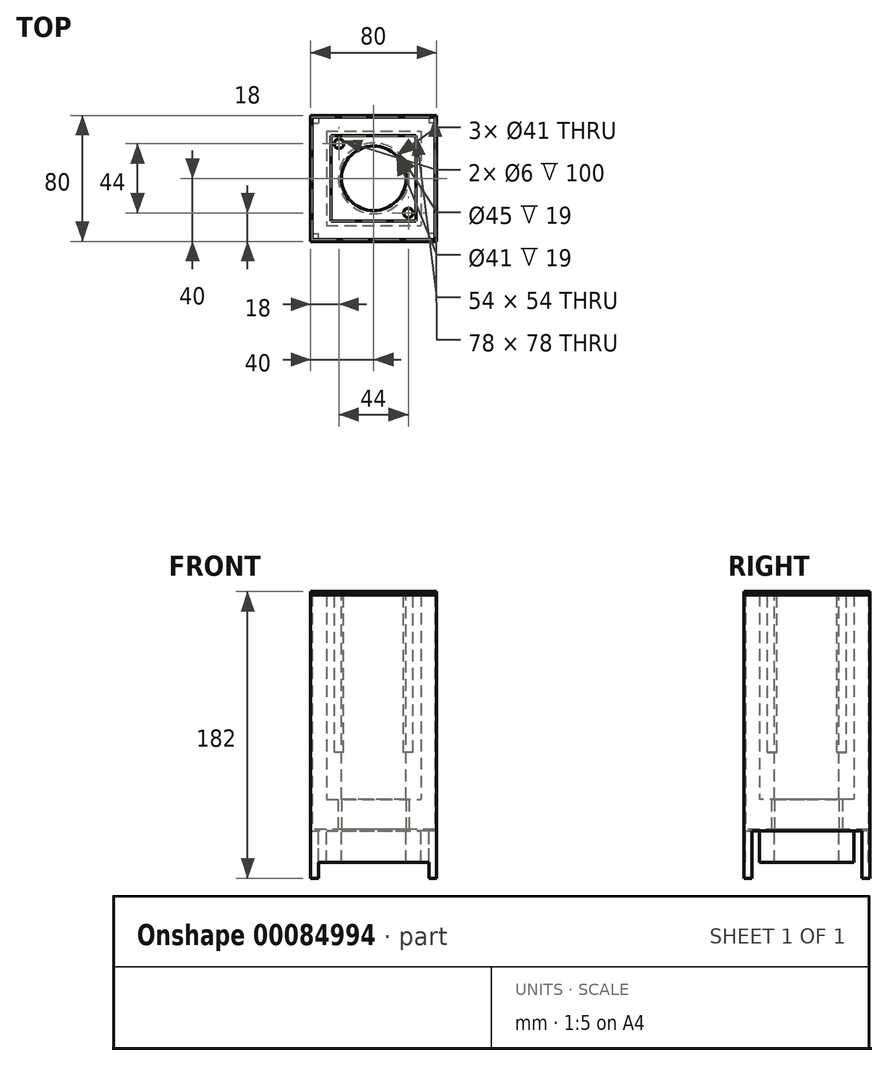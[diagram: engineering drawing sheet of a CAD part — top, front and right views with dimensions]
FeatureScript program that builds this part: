
annotation { "Feature Type Name" : "Feature", "Feature Type Description" : "" }
export const myFeature = defineFeature(function(context is Context, id is Id, definition is map)
    precondition{}
    {
        {
            var Q0;
            Q0=qCreatedBy(makeId("Top.planeOp"),FACE);
            var sketch = newSketch(context, id + "F0", { "sketchPlane" : qUnion([Q0])});
            skLineSegment(sketch, "E0.bottom", {"start": v(-30, 30) * mm, "end": v(30, 30) * mm});
            skLineSegment(sketch, "E0.top", {"start": v(-30, -30) * mm, "end": v(30, -30) * mm});
            skLineSegment(sketch, "E0.left", {"start": v(-30, 30) * mm, "end": v(-30, -30) * mm});
            skLineSegment(sketch, "E0.right", {"start": v(30, 30) * mm, "end": v(30, -30) * mm});
            skSolve(sketch);
        }
        {
            var Q0;
            Q0 = qSketchRegion(id + "F0", true);
            extrude(context, id + "F1", {"entities" : qUnion([Q0]), "depth" : 130 * mm});
        }
        {
            var Q0;
            Q0=makeQuery(id+"F1.opExtrude","CAP_FACE",FACE,{"disambiguationData":[OSD([sQuery(id+"F0.wireOp",EDGE,"E0.bottom"),sQuery(id+"F0.wireOp",EDGE,"E0.top"),sQuery(id+"F0.wireOp",EDGE,"E0.left"),sQuery(id+"F0.wireOp",EDGE,"E0.right")])],"isStart":false});
            var sketch = newSketch(context, id + "F2", { "sketchPlane" : qUnion([Q0])});
            skCircle(sketch, "E1", {"center": v(0, 0) * mm, "radius": 20.5 * mm});
            skSolve(sketch);
        }
        {
            var Q0;
            Q0=makeQuery(id+"F2.imprint","IMPRINT",FACE,{"disambiguationData":[TD([[makeQuery(id+"F2.imprint","IMPRINT",EDGE,{"derivedFrom":sQuery(id+"F2.wireOp",EDGE,"E1")}),1.0]])]});
            extrude(context, id + "F3", {"entities" : qUnion([Q0]), "operationType" : NewBodyOperationType.REMOVE, "oppositeDirection" : true, "depth" : 150 * mm});
        }
        {
            var Q0;
            Q0=makeQuery(id+"F1.opExtrude","CAP_FACE",FACE,{"disambiguationData":[OSD([sQuery(id+"F0.wireOp",EDGE,"E0.bottom"),sQuery(id+"F0.wireOp",EDGE,"E0.top"),sQuery(id+"F0.wireOp",EDGE,"E0.left"),sQuery(id+"F0.wireOp",EDGE,"E0.right")])],"isStart":false});
            var sketch = newSketch(context, id + "F4", { "sketchPlane" : qUnion([Q0])});
            skCircle(sketch, "E2", {"center": v(22, -22) * mm, "radius": 3 * mm});
            skCircle(sketch, "E3", {"center": v(-22, 22) * mm, "radius": 3 * mm});
            skSolve(sketch);
        }
        {
            var Q0;
            Q0=makeQuery(id+"F4.imprint","IMPRINT",FACE,{"disambiguationData":[TD([[makeQuery(id+"F4.imprint","IMPRINT",EDGE,{"derivedFrom":sQuery(id+"F4.wireOp",EDGE,"E3")}),1.0]])]});
            var Q1;
            Q1=makeQuery(id+"F4.imprint","IMPRINT",FACE,{"disambiguationData":[TD([[makeQuery(id+"F4.imprint","IMPRINT",EDGE,{"derivedFrom":sQuery(id+"F4.wireOp",EDGE,"E2")}),1.0]])]});
            extrude(context, id + "F5", {"entities" : qUnion([Q0, Q1]), "operationType" : NewBodyOperationType.REMOVE, "oppositeDirection" : true, "depth" : 100 * mm});
        }
        {
            var Q0;
            Q0 = qSketchRegion(id + "F4", true);
            extrude(context, id + "F6", {"entities" : qUnion([Q0]), "oppositeDirection" : true, "depth" : 100 * mm});
        }
        {
            var Q0;
            Q0=qCreatedBy(makeId("Top.planeOp"),FACE);
            var sketch = newSketch(context, id + "F7", { "sketchPlane" : qUnion([Q0])});
            skLineSegment(sketch, "E4.bottom", {"start": v(40, 40) * mm, "end": v(-40, 40) * mm});
            skLineSegment(sketch, "E4.top", {"start": v(40, -40) * mm, "end": v(-40, -40) * mm});
            skLineSegment(sketch, "E4.left", {"start": v(40, 40) * mm, "end": v(40, -40) * mm});
            skLineSegment(sketch, "E4.right", {"start": v(-40, 40) * mm, "end": v(-40, -40) * mm});
            skSolve(sketch);
        }
        {
            var Q0;
            Q0=makeQuery(id+"F7.imprint","IMPRINT",FACE,{"disambiguationData":[TD([[makeQuery(id+"F7.imprint","IMPRINT",EDGE,{"derivedFrom":sQuery(id+"F7.wireOp",EDGE,"E4.bottom")}),1.0]])]});
            extrude(context, id + "F8", {"entities" : qUnion([Q0]), "depth" : 130 * mm, "hasSecondDirection" : true, "secondDirectionOppositeDirection" : true, "secondDirectionDepth" : 20 * mm});
        }
        {
            var Q0;
            Q0=makeQuery(id+"F8.opExtrude","CAP_FACE",FACE,{"disambiguationData":[OSD([sQuery(id+"F7.wireOp",EDGE,"E4.bottom"),sQuery(id+"F7.wireOp",EDGE,"E4.top"),sQuery(id+"F7.wireOp",EDGE,"E4.left"),sQuery(id+"F7.wireOp",EDGE,"E4.right")])],"isStart":false});
            shell(context, id + "F9", {"entities" : qUnion([Q0]), "thickness" : 1 * mm});
        }
        {
            var Q0;
            Q0=makeQuery(id+"F8.opExtrude","CAP_FACE",FACE,{"disambiguationData":[OSD([sQuery(id+"F7.wireOp",EDGE,"E4.bottom"),sQuery(id+"F7.wireOp",EDGE,"E4.top"),sQuery(id+"F7.wireOp",EDGE,"E4.left"),sQuery(id+"F7.wireOp",EDGE,"E4.right")])],"isStart":true});
            var sketch = newSketch(context, id + "F10", { "sketchPlane" : qUnion([Q0])});
            skCircle(sketch, "E5", {"center": v(0, 0) * mm, "radius": 20.5 * mm});
            skSolve(sketch);
        }
        {
            var Q0;
            Q0=makeQuery(id+"F10.imprint","IMPRINT",FACE,{"disambiguationData":[TD([[makeQuery(id+"F10.imprint","IMPRINT",EDGE,{"derivedFrom":sQuery(id+"F10.wireOp",EDGE,"E5")}),1.0]])]});
            extrude(context, id + "F11", {"entities" : qUnion([Q0]), "operationType" : NewBodyOperationType.REMOVE, "oppositeDirection" : true, "depth" : 25 * mm});
        }
        {
            var Q0;
            Q0=makeQuery(id+"F9.opShell","OFFSET_FACE",FACE,{"disambiguationData":[OSD([sQuery(id+"F7.wireOp",EDGE,"E4.bottom"),sQuery(id+"F7.wireOp",EDGE,"E4.top"),sQuery(id+"F7.wireOp",EDGE,"E4.left"),sQuery(id+"F7.wireOp",EDGE,"E4.right")])]});
            var sketch = newSketch(context, id + "F12", { "sketchPlane" : qUnion([Q0])});
            skCircle(sketch, "E6", {"center": v(0, 0) * mm, "radius": 22.5 * mm});
            skCircle(sketch, "E7", {"center": v(0, 0) * mm, "radius": 20.5 * mm});
            skSolve(sketch);
        }
        {
            var Q0;
            Q0=makeQuery(id+"F12.imprint","IMPRINT",FACE,{"disambiguationData":[TD([[makeQuery(id+"F12.imprint","IMPRINT",EDGE,{"derivedFrom":sQuery(id+"F12.wireOp",EDGE,"E6")}),1.0]])]});
            extrude(context, id + "F13", {"entities" : qUnion([Q0]), "depth" : 19 * mm});
        }
        {
            var Q0;
            Q0=makeQuery(id+"F8.opExtrude","CAP_FACE",FACE,{"disambiguationData":[OSD([sQuery(id+"F7.wireOp",EDGE,"E4.bottom"),sQuery(id+"F7.wireOp",EDGE,"E4.top"),sQuery(id+"F7.wireOp",EDGE,"E4.left"),sQuery(id+"F7.wireOp",EDGE,"E4.right")])],"isStart":true});
            var sketch = newSketch(context, id + "F14", { "sketchPlane" : qUnion([Q0])});
            skLineSegment(sketch, "E8.0", {"start": v(30, -30) * mm, "end": v(30, 30) * mm});
            skLineSegment(sketch, "E8.1", {"start": v(-30, -30) * mm, "end": v(30, -30) * mm});
            skLineSegment(sketch, "E8.2", {"start": v(-30, 30) * mm, "end": v(-30, -30) * mm});
            skLineSegment(sketch, "E8.3", {"start": v(30, 30) * mm, "end": v(-30, 30) * mm});
            skSolve(sketch);
        }
        {
            var Q0;
            Q0=makeQuery(id+"F14.imprint","IMPRINT",FACE,{"disambiguationData":[TD([[makeQuery(id+"F14.imprint","IMPRINT",EDGE,{"derivedFrom":sQuery(id+"F14.wireOp",EDGE,"E8.0")}),1.0]])]});
            var Q1;
            Q1=makeQuery(id+"F14.imprint","IMPRINT",FACE,{"disambiguationData":[TD([[makeQuery(id+"F14.imprint","IMPRINT",EDGE,{"derivedFrom":makeQuery(id+"F11.boolean.opBoolean","COPY",EDGE,{"derivedFrom":makeQuery(id+"F11.opExtrude","CAP_EDGE",EDGE,{"disambiguationData":[OSD([sQuery(id+"F10.wireOp",EDGE,"E5")])],"isStart":true})})}),1.0]])]});
            extrude(context, id + "F15", {"entities" : qUnion([Q0, Q1]), "depth" : 20 * mm});
        }
        {
            var Q0;
            Q0=makeQuery(id+"F8.opExtrude","CAP_FACE",FACE,{"disambiguationData":[OSD([sQuery(id+"F7.wireOp",EDGE,"E4.bottom"),sQuery(id+"F7.wireOp",EDGE,"E4.top"),sQuery(id+"F7.wireOp",EDGE,"E4.left"),sQuery(id+"F7.wireOp",EDGE,"E4.right")])],"isStart":true});
            var sketch = newSketch(context, id + "F16", { "sketchPlane" : qUnion([Q0])});
            skLineSegment(sketch, "E9.bottom", {"start": v(40, -40) * mm, "end": v(35, -40) * mm});
            skLineSegment(sketch, "E9.top", {"start": v(40, -35) * mm, "end": v(35, -35) * mm});
            skLineSegment(sketch, "E9.left", {"start": v(40, -40) * mm, "end": v(40, -35) * mm});
            skLineSegment(sketch, "E9.right", {"start": v(35, -40) * mm, "end": v(35, -35) * mm});
            skLineSegment(sketch, "E10.bottom", {"start": v(-40, -40) * mm, "end": v(-35, -40) * mm});
            skLineSegment(sketch, "E10.top", {"start": v(-40, -35) * mm, "end": v(-35, -35) * mm});
            skLineSegment(sketch, "E10.left", {"start": v(-40, -40) * mm, "end": v(-40, -35) * mm});
            skLineSegment(sketch, "E10.right", {"start": v(-35, -40) * mm, "end": v(-35, -35) * mm});
            skLineSegment(sketch, "E11.bottom", {"start": v(-40, 40) * mm, "end": v(-35, 40) * mm});
            skLineSegment(sketch, "E11.top", {"start": v(-40, 35) * mm, "end": v(-35, 35) * mm});
            skLineSegment(sketch, "E11.left", {"start": v(-40, 40) * mm, "end": v(-40, 35) * mm});
            skLineSegment(sketch, "E11.right", {"start": v(-35, 40) * mm, "end": v(-35, 35) * mm});
            skLineSegment(sketch, "E12.bottom", {"start": v(40, 40) * mm, "end": v(35, 40) * mm});
            skLineSegment(sketch, "E12.top", {"start": v(40, 35) * mm, "end": v(35, 35) * mm});
            skLineSegment(sketch, "E12.left", {"start": v(40, 40) * mm, "end": v(40, 35) * mm});
            skLineSegment(sketch, "E12.right", {"start": v(35, 40) * mm, "end": v(35, 35) * mm});
            skLineSegment(sketch, "E13.bottom", {"start": v(40, -35) * mm, "end": v(37.5, -35) * mm});
            skLineSegment(sketch, "E13.top", {"start": v(40, 35) * mm, "end": v(37.5, 35) * mm});
            skLineSegment(sketch, "E14.bottom", {"start": v(-40, -35) * mm, "end": v(-39, -35) * mm});
            skLineSegment(sketch, "E14.top", {"start": v(-40, 35) * mm, "end": v(-39, 35) * mm});
            skLineSegment(sketch, "E14.left", {"start": v(-40, -35) * mm, "end": v(-40, 35) * mm});
            skLineSegment(sketch, "E14.right", {"start": v(-39, -35) * mm, "end": v(-39, 35) * mm});
            skLineSegment(sketch, "E15.bottom", {"start": v(40, 35) * mm, "end": v(39, 35) * mm});
            skLineSegment(sketch, "E15.top", {"start": v(40, -35) * mm, "end": v(39, -35) * mm});
            skLineSegment(sketch, "E15.left", {"start": v(40, 35) * mm, "end": v(40, -35) * mm});
            skLineSegment(sketch, "E15.right", {"start": v(39, 35) * mm, "end": v(39, -35) * mm});
            skLineSegment(sketch, "E16.bottom", {"start": v(-35, -40) * mm, "end": v(35, -40) * mm});
            skLineSegment(sketch, "E16.top", {"start": v(-35, -39) * mm, "end": v(35, -39) * mm});
            skLineSegment(sketch, "E16.left", {"start": v(-35, -40) * mm, "end": v(-35, -39) * mm});
            skLineSegment(sketch, "E16.right", {"start": v(35, -40) * mm, "end": v(35, -39) * mm});
            skLineSegment(sketch, "E17.bottom", {"start": v(35, 40) * mm, "end": v(-35, 40) * mm});
            skLineSegment(sketch, "E17.top", {"start": v(35, 39) * mm, "end": v(-35, 39) * mm});
            skLineSegment(sketch, "E17.left", {"start": v(35, 40) * mm, "end": v(35, 39) * mm});
            skLineSegment(sketch, "E17.right", {"start": v(-35, 40) * mm, "end": v(-35, 39) * mm});
            skSolve(sketch);
        }
        {
            var Q0;
            Q0=makeQuery(id+"F16.imprint","IMPRINT",FACE,{"disambiguationData":[TD([[makeQuery(id+"F16.imprint","IMPRINT",EDGE,{"derivedFrom":sQuery(id+"F16.wireOp",EDGE,"E9.bottom")}),-1.0]])]});
            var Q1;
            Q1=makeQuery(id+"F16.imprint","IMPRINT",FACE,{"disambiguationData":[TD([[makeQuery(id+"F16.imprint","IMPRINT",EDGE,{"derivedFrom":sQuery(id+"F16.wireOp",EDGE,"E10.bottom")}),-1.0]])]});
            var Q2;
            Q2=makeQuery(id+"F16.imprint","IMPRINT",FACE,{"disambiguationData":[TD([[makeQuery(id+"F16.imprint","IMPRINT",EDGE,{"derivedFrom":sQuery(id+"F16.wireOp",EDGE,"E11.bottom")}),1.0]])]});
            var Q3;
            Q3=makeQuery(id+"F16.imprint","IMPRINT",FACE,{"disambiguationData":[TD([[makeQuery(id+"F16.imprint","IMPRINT",EDGE,{"derivedFrom":sQuery(id+"F16.wireOp",EDGE,"E12.bottom")}),1.0]])]});
            extrude(context, id + "F17", {"entities" : qUnion([Q0, Q1, Q2, Q3]), "operationType" : NewBodyOperationType.ADD, "depth" : 30 * mm});
        }
        {
            var Q0;
            Q0=makeQuery(id+"F16.imprint","IMPRINT",FACE,{"disambiguationData":[TD([[makeQuery(id+"F16.imprint","IMPRINT",EDGE,{"derivedFrom":sQuery(id+"F16.wireOp",EDGE,"E15.bottom")}),1.0]])]});
            var Q1;
            Q1=makeQuery(id+"F16.imprint","IMPRINT",FACE,{"disambiguationData":[TD([[makeQuery(id+"F16.imprint","IMPRINT",EDGE,{"derivedFrom":sQuery(id+"F16.wireOp",EDGE,"E16.bottom")}),-1.0]])]});
            var Q2;
            Q2=makeQuery(id+"F16.imprint","IMPRINT",FACE,{"disambiguationData":[TD([[makeQuery(id+"F16.imprint","IMPRINT",EDGE,{"derivedFrom":sQuery(id+"F16.wireOp",EDGE,"E14.bottom")}),1.0]])]});
            var Q3;
            Q3=makeQuery(id+"F16.imprint","IMPRINT",FACE,{"disambiguationData":[TD([[makeQuery(id+"F16.imprint","IMPRINT",EDGE,{"derivedFrom":sQuery(id+"F16.wireOp",EDGE,"E17.bottom")}),1.0]])]});
            extrude(context, id + "F18", {"entities" : qUnion([Q0, Q1, Q2, Q3]), "operationType" : NewBodyOperationType.ADD, "depth" : 20 * mm});
        }
        {
            var Q0;
            Q0=makeQuery(id+"F9.opShell","OFFSET_FACE",FACE,{"disambiguationData":[OSD([sQuery(id+"F7.wireOp",EDGE,"E4.bottom"),sQuery(id+"F7.wireOp",EDGE,"E4.top"),sQuery(id+"F7.wireOp",EDGE,"E4.left"),sQuery(id+"F7.wireOp",EDGE,"E4.right")])]});
            extrude(context, id + "F19", {"entities" : qUnion([Q0]), "depth" : 149 * mm});
        }
        {
            var Q0;
            Q0=makeQuery(id+"F15.opExtrude","SWEPT_BODY",BODY,{"disambiguationData":[OSD([sQuery(id+"F14.wireOp",EDGE,"E8.0"),sQuery(id+"F14.wireOp",EDGE,"E8.1"),sQuery(id+"F14.wireOp",EDGE,"E8.2"),sQuery(id+"F14.wireOp",EDGE,"E8.3")])]});
            var Q1;
            Q1=makeQuery(id+"F13.opExtrude","SWEPT_BODY",BODY,{"disambiguationData":[OSD([sQuery(id+"F12.wireOp",EDGE,"E6"),sQuery(id+"F12.wireOp",EDGE,"E7")])]});
            var Q2;
            Q2=makeQuery(id+"F6.opExtrude","SWEPT_BODY",BODY,{"disambiguationData":[OSD([sQuery(id+"F4.wireOp",EDGE,"E3")])]});
            var Q3;
            Q3=makeQuery(id+"F8.opExtrude","SWEPT_BODY",BODY,{"disambiguationData":[OSD([sQuery(id+"F7.wireOp",EDGE,"E4.bottom"),sQuery(id+"F7.wireOp",EDGE,"E4.top"),sQuery(id+"F7.wireOp",EDGE,"E4.left"),sQuery(id+"F7.wireOp",EDGE,"E4.right")])]});
            var Q4;
            Q4=makeQuery(id+"F6.opExtrude","SWEPT_BODY",BODY,{"disambiguationData":[OSD([sQuery(id+"F4.wireOp",EDGE,"E2")])]});
            var Q5;
            Q5=makeQuery(id+"F1.opExtrude","SWEPT_BODY",BODY,{"disambiguationData":[OSD([sQuery(id+"F0.wireOp",EDGE,"E0.bottom"),sQuery(id+"F0.wireOp",EDGE,"E0.top"),sQuery(id+"F0.wireOp",EDGE,"E0.left"),sQuery(id+"F0.wireOp",EDGE,"E0.right")])]});
            var Q6;
            Q6=makeQuery(id+"F19.opExtrude","SWEPT_BODY",BODY,{"disambiguationData":[OSD([sQuery(id+"F7.wireOp",EDGE,"E4.bottom"),sQuery(id+"F7.wireOp",EDGE,"E4.top"),sQuery(id+"F7.wireOp",EDGE,"E4.left"),sQuery(id+"F7.wireOp",EDGE,"E4.right")])]});
            booleanBodies(context, id + "F20", {"operationType" : BooleanOperationType.SUBTRACTION, "tools" : qUnion([Q0, Q1, Q2, Q3, Q4, Q5]), "targets" : qUnion([Q6]), "keepTools" : true});
        }
        {
            var Q0;
            Q0=makeQuery(id+"F19.opExtrude","CAP_FACE",FACE,{"disambiguationData":[OSD([sQuery(id+"F7.wireOp",EDGE,"E4.bottom"),sQuery(id+"F7.wireOp",EDGE,"E4.top"),sQuery(id+"F7.wireOp",EDGE,"E4.left"),sQuery(id+"F7.wireOp",EDGE,"E4.right")])],"isStart":false});
            var sketch = newSketch(context, id + "F21", { "sketchPlane" : qUnion([Q0])});
            skLineSegment(sketch, "E18.0", {"start": v(27, 27) * mm, "end": v(-27, 27) * mm});
            skLineSegment(sketch, "E18.1", {"start": v(27, -27) * mm, "end": v(27, 27) * mm});
            skLineSegment(sketch, "E18.2", {"start": v(-27, -27) * mm, "end": v(27, -27) * mm});
            skLineSegment(sketch, "E18.3", {"start": v(-27, 27) * mm, "end": v(-27, -27) * mm});
            skLineSegment(sketch, "E19.bottom", {"start": v(-40, 40) * mm, "end": v(40, 40) * mm});
            skLineSegment(sketch, "E19.top", {"start": v(-40, -38.85) * mm, "end": v(38.83, -38.85) * mm});
            skLineSegment(sketch, "E19.left", {"start": v(-40, 40) * mm, "end": v(-40, -38.85) * mm});
            skLineSegment(sketch, "E19.right", {"start": v(40, 40) * mm, "end": v(40, -40) * mm});
            skSolve(sketch);
        }
        {
            var Q0;
            Q0=makeQuery(id+"F8.opExtrude","CAP_FACE",FACE,{"disambiguationData":[OSD([sQuery(id+"F7.wireOp",EDGE,"E4.bottom"),sQuery(id+"F7.wireOp",EDGE,"E4.top"),sQuery(id+"F7.wireOp",EDGE,"E4.left"),sQuery(id+"F7.wireOp",EDGE,"E4.right")])],"isStart":false});
            var Q1;
            Q1=makeQuery(id+"F21.imprint","IMPRINT",FACE,{"disambiguationData":[TD([[makeQuery(id+"F21.imprint","IMPRINT",EDGE,{"derivedFrom":makeQuery(id+"F19.opExtrude","CAP_EDGE",EDGE,{"disambiguationData":[OSD([sQuery(id+"F7.wireOp",EDGE,"E4.bottom")])],"isStart":false})}),1.0]])]});
            var Q2;
            Q2=makeQuery(id+"F21.imprint","IMPRINT",FACE,{"disambiguationData":[TD([[makeQuery(id+"F21.imprint","IMPRINT",EDGE,{"derivedFrom":sQuery(id+"F21.wireOp",EDGE,"E18.0")}),-1.0]])]});
            extrude(context, id + "F22", {"entities" : qUnion([Q0, Q1, Q2]), "depth" : 2 * mm});
        }
    });
